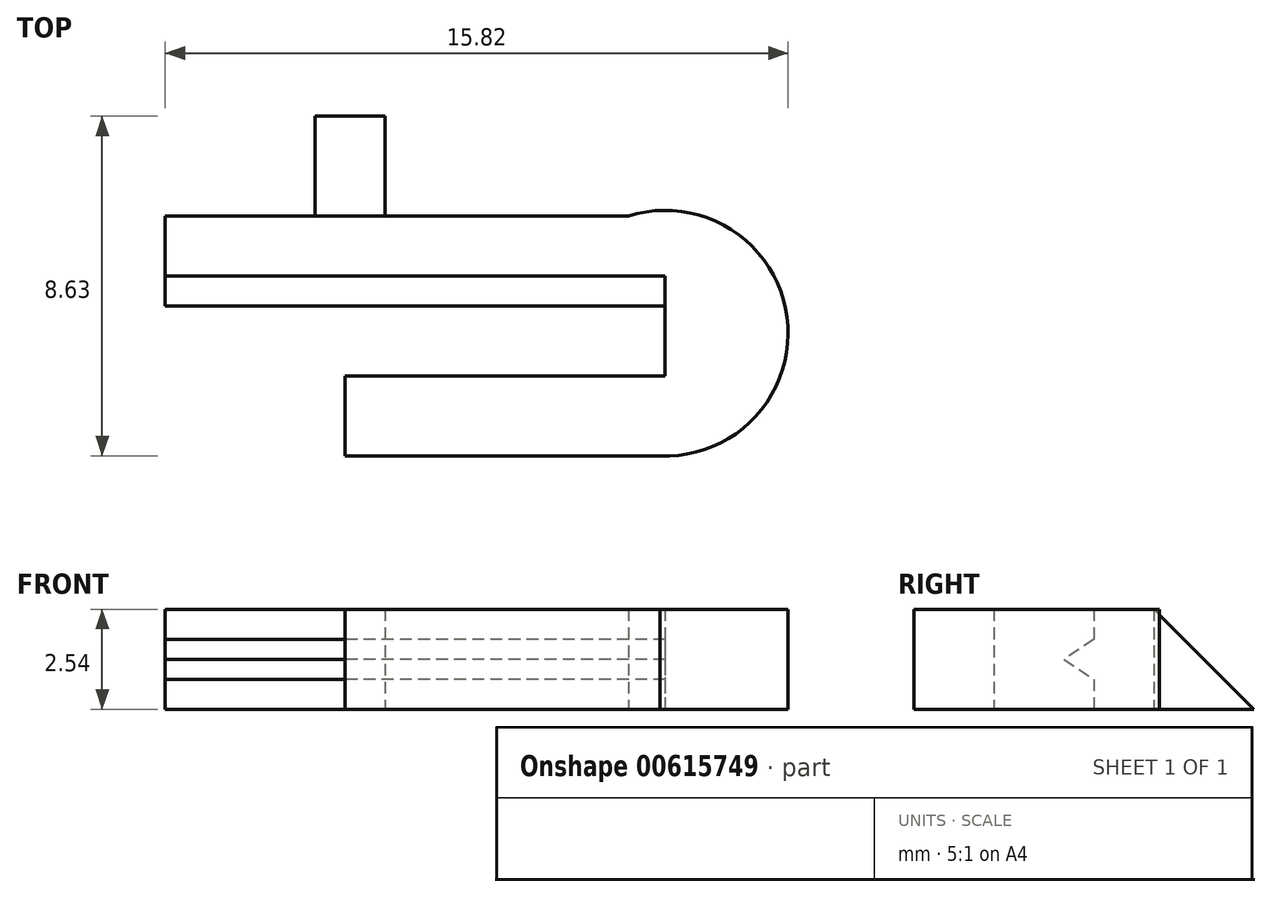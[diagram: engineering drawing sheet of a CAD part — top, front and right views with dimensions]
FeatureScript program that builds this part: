
annotation { "Feature Type Name" : "Feature", "Feature Type Description" : "" }
export const myFeature = defineFeature(function(context is Context, id is Id, definition is map)
    precondition{}
    {
        {
            var Q0;
            Q0=qCreatedBy(makeId("Top.planeOp"),FACE);
            var sketch = newSketch(context, id + "F0", { "sketchPlane" : qUnion([Q0])});
            skLineSegment(sketch, "E0", {"start": v(0, 0) * mm, "end": v(12.7, 0) * mm});
            skLineSegment(sketch, "E1", {"start": v(12.7, 0) * mm, "end": v(12.7, -2.54) * mm});
            skLineSegment(sketch, "E2", {"start": v(12.7, -2.54) * mm, "end": v(4.57, -2.54) * mm});
            skLineSegment(sketch, "E3", {"start": v(4.57, -2.54) * mm, "end": v(4.57, -4.57) * mm});
            skLineSegment(sketch, "E4", {"start": v(4.57, -4.57) * mm, "end": v(12.57, -4.57) * mm});
            skLineSegment(sketch, "E5", {"start": v(0, 0) * mm, "end": v(0, 1.52) * mm});
            skLineSegment(sketch, "E6", {"start": v(0, 1.52) * mm, "end": v(11.76, 1.52) * mm});
            skArc(sketch, "E7", {"start": v(12.57, -4.57) * mm, "mid": v(15.8, -1.04) * mm, "end": v(11.76, 1.52) * mm});
            skSolve(sketch);
        }
        {
            var Q0;
            Q0=qSketchRegion(id+"F0",true);
            extrude(context, id + "F1", {"entities" : qUnion([Q0]), "endBound" : BoundingType.SYMMETRIC, "depth" : 2.54 * mm, "offsetDistance" : 25.4 * mm});
        }
        {
            var Q0;
            Q0=makeQuery(id+"F1.opExtrude","SWEPT_FACE",FACE,{"disambiguationData":[OSD([sQuery(id+"F0.wireOp",EDGE,"E5")])]});
            var sketch = newSketch(context, id + "F2", { "sketchPlane" : qUnion([Q0])});
            skLineSegment(sketch, "E8", {"start": v(0, 0.5) * mm, "end": v(0.76, 0) * mm});
            skLineSegment(sketch, "E9", {"start": v(0.76, 0) * mm, "end": v(0, -0.5) * mm});
            skLineSegment(sketch, "E10", {"start": v(0, -0.5) * mm, "end": v(0, 0.5) * mm});
            skSolve(sketch);
        }
        {
            var Q0;
            Q0=qSketchRegion(id+"F2",true);
            extrude(context, id + "F3", {"entities" : qUnion([Q0]), "operationType" : NewBodyOperationType.ADD, "endBound" : BoundingType.UP_TO_NEXT, "oppositeDirection" : true, "depth" : 25.4 * mm, "offsetDistance" : 25.4 * mm});
        }
        {
            var Q0;
            Q0=makeQuery(id+"F6.boolean.opBoolean","MERGE",FACE,{"derivedFrom":[makeQuery(id+"F3.boolean.opBoolean","MERGE",FACE,{"derivedFrom":[makeQuery(id+"F1.opExtrude","SWEPT_FACE",FACE,{"disambiguationData":[OSD([sQuery(id+"F0.wireOp",EDGE,"E5")])]}),makeQuery(id+"F3.opExtrude","CAP_FACE",FACE,{"disambiguationData":[OSD([sQuery(id+"F2.wireOp",EDGE,"E8"),sQuery(id+"F2.wireOp",EDGE,"E9"),sQuery(id+"F2.wireOp",EDGE,"E10")])],"isStart":true})]}),makeQuery(id+"F6.opExtrude","CAP_FACE",FACE,{"disambiguationData":[OSD([sQuery(id+"F5.wireOp",EDGE,"E11"),sQuery(id+"F5.wireOp",EDGE,"E12"),sQuery(id+"F5.wireOp",EDGE,"E13")])],"isStart":true})]});
            cPlane(context, id + "F4", {"entities" : qUnion([Q0]), "cplaneType" : CPlaneType.OFFSET, "offset" : 3.8 * mm, "oppositeDirection" : true, "width" : 152.4 * mm, "height" : 152.4 * mm});
        }
        {
            var Q0;
            Q0=qCreatedBy(id+"F4.planeOp",FACE);
            var sketch = newSketch(context, id + "F5", { "sketchPlane" : qUnion([Q0])});
            skLineSegment(sketch, "E11", {"start": v(-1.52, -1.27) * mm, "end": v(-4.06, -1.27) * mm});
            skLineSegment(sketch, "E12", {"start": v(-4.06, -1.27) * mm, "end": v(-1.52, 1.27) * mm});
            skLineSegment(sketch, "E13", {"start": v(-1.52, 1.27) * mm, "end": v(-1.52, -1.27) * mm});
            skSolve(sketch);
        }
        {
            var Q0;
            Q0=qSketchRegion(id+"F5",true);
            extrude(context, id + "F6", {"entities" : qUnion([Q0]), "operationType" : NewBodyOperationType.ADD, "oppositeDirection" : true, "depth" : 1.78 * mm, "offsetDistance" : 25.4 * mm});
        }
    });
